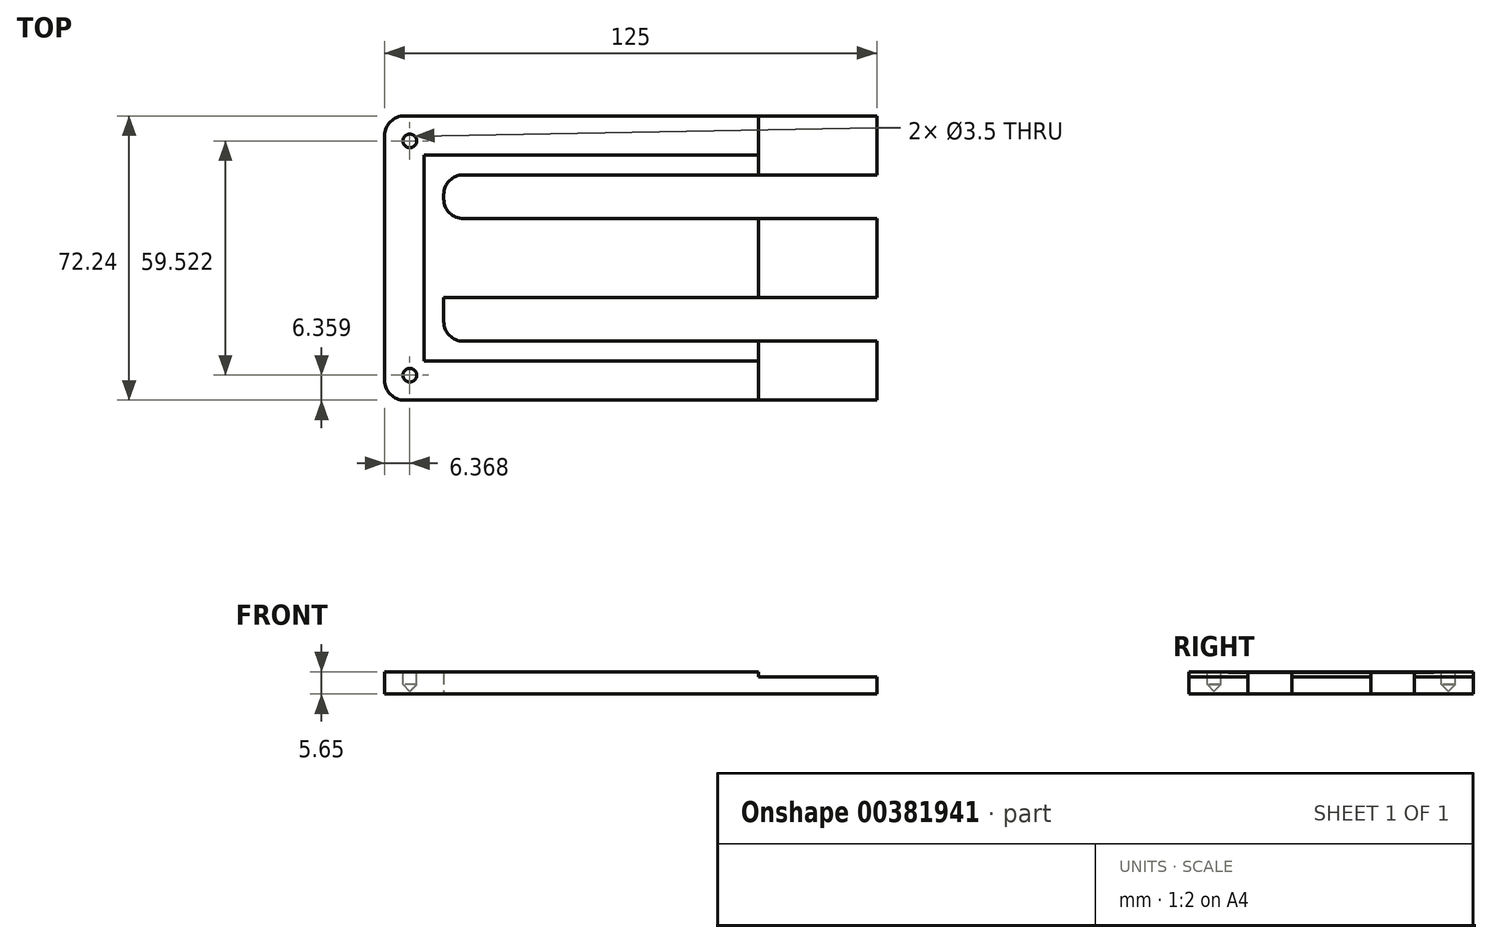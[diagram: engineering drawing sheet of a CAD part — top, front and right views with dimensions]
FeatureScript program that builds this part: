
annotation { "Feature Type Name" : "Feature", "Feature Type Description" : "" }
export const myFeature = defineFeature(function(context is Context, id is Id, definition is map)
    precondition{}
    {
        {
            var Q0;
            Q0=qCreatedBy(makeId("Top.planeOp"),FACE);
            var sketch = newSketch(context, id + "F0", { "sketchPlane" : qUnion([Q0])});
            skLineSegment(sketch, "E0.bottom", {"start": v(-143.35, 36.12) * mm, "end": v(86.65, 36.13) * mm});
            skLineSegment(sketch, "E0.top", {"start": v(-143.35, -36.13) * mm, "end": v(86.65, -36.12) * mm});
            skLineSegment(sketch, "E0.left", {"start": v(-143.35, 36.12) * mm, "end": v(-143.35, -36.13) * mm});
            skLineSegment(sketch, "E0.right", {"start": v(86.65, 36.13) * mm, "end": v(86.65, -36.12) * mm});
            skLineSegment(sketch, "E1.bottom", {"start": v(-128.35, 21.12) * mm, "end": v(71.65, 21.13) * mm});
            skLineSegment(sketch, "E1.top", {"start": v(-128.35, -21.13) * mm, "end": v(71.65, -21.12) * mm});
            skLineSegment(sketch, "E1.left", {"start": v(-128.35, 21.12) * mm, "end": v(-128.35, -21.13) * mm});
            skLineSegment(sketch, "E1.right", {"start": v(71.65, 21.13) * mm, "end": v(71.65, -21.12) * mm});
            skLineSegment(sketch, "E2.bottom", {"start": v(-133.35, 26.12) * mm, "end": v(76.65, 26.13) * mm});
            skLineSegment(sketch, "E2.top", {"start": v(-133.35, -26.13) * mm, "end": v(76.65, -26.12) * mm});
            skLineSegment(sketch, "E2.left", {"start": v(-133.35, 26.12) * mm, "end": v(-133.35, -26.13) * mm});
            skLineSegment(sketch, "E2.right", {"start": v(76.65, 26.13) * mm, "end": v(76.65, -26.12) * mm});
            skSolve(sketch);
        }
        {
            var Q0;
            Q0=makeQuery(id+"F0.imprint","IMPRINT",FACE,{"disambiguationData":[TD([[makeQuery(id+"F0.imprint","IMPRINT",EDGE,{"derivedFrom":sQuery(id+"F0.wireOp",EDGE,"E1.bottom")}),1.0]])]});
            extrude(context, id + "F1", {"entities" : qUnion([Q0]), "depth" : 5.5 * mm});
        }
        {
            var Q0;
            Q0=makeQuery(id+"F0.imprint","IMPRINT",FACE,{"disambiguationData":[TD([[makeQuery(id+"F0.imprint","IMPRINT",EDGE,{"derivedFrom":sQuery(id+"F0.wireOp",EDGE,"E0.bottom")}),-1.0]])]});
            extrude(context, id + "F2", {"entities" : qUnion([Q0]), "operationType" : NewBodyOperationType.ADD, "depth" : 5.65 * mm});
        }
        {
            var Q0;
            Q0=makeQuery(id+"F2.opExtrude","SWEPT_FACE",FACE,{"disambiguationData":[OSD([sQuery(id+"F0.wireOp",EDGE,"E0.top")])]});
            var sketch = newSketch(context, id + "F3", { "sketchPlane" : qUnion([Q0])});
            skPoint(sketch, "E3.orphan", {"position": v(66.65, 1.3) * mm});
            skPoint(sketch, "E4.start.orphan", {"position": v(-133.35, 1.3) * mm});
            skLineSegment(sketch, "E5", {"start": v(-48.35, 4.35) * mm, "end": v(-48.35, 5.65) * mm});
            skLineSegment(sketch, "E6", {"start": v(-18.35, 4.35) * mm, "end": v(-18.35, 0) * mm});
            skPoint(sketch, "E7.start.orphan", {"position": v(-13.35, 1.3) * mm});
            skPoint(sketch, "E8.end.orphan", {"position": v(-28.35, 5.65) * mm});
            skPoint(sketch, "E9.start.orphan", {"position": v(-33.35, 1.3) * mm});
            skLineSegment(sketch, "E10", {"start": v(-48.35, 4.35) * mm, "end": v(-18.35, 4.35) * mm});
            skSolve(sketch);
        }
        {
            var Q0;
            {var subQ3=sQuery(id+"F3.wireOp",EDGE,"E5");Q0=makeQuery(id+"F3.imprint","IMPRINT",FACE,{"disambiguationData":[TD([[makeQuery(id+"F3.imprint","IMPRINT",EDGE,{"derivedFrom":subQ3}),-1.0]])]});}
            extrude(context, id + "F4", {"entities" : qUnion([Q0]), "operationType" : NewBodyOperationType.REMOVE, "oppositeDirection" : true, "depth" : 100 * mm});
        }
        {
            var Q0;
            Q0=makeQuery(id+"F2.opExtrude","CAP_FACE",FACE,{"disambiguationData":[OSD([sQuery(id+"F0.wireOp",EDGE,"E0.bottom"),sQuery(id+"F0.wireOp",EDGE,"E0.top"),sQuery(id+"F0.wireOp",EDGE,"E0.left"),sQuery(id+"F0.wireOp",EDGE,"E0.right"),sQuery(id+"F0.wireOp",EDGE,"E2.bottom"),sQuery(id+"F0.wireOp",EDGE,"E2.top"),sQuery(id+"F0.wireOp",EDGE,"E2.left"),sQuery(id+"F0.wireOp",EDGE,"E2.right")])],"isStart":false});
            var sketch = newSketch(context, id + "F5", { "sketchPlane" : qUnion([Q0])});
            skLineSegment(sketch, "E11", {"start": v(-143.35, -36.13) * mm, "end": v(-133.35, -26.13) * mm});
            skCircle(sketch, "E12", {"center": v(-136.98, -29.76) * mm, "radius": 1.75 * mm});
            skLineSegment(sketch, "E13.MirrorCS", {"start": v(-143.35, 36.13) * mm, "end": v(-133.35, 26.13) * mm});
            skCircle(sketch, "E14.MirrorC", {"center": v(-136.98, 29.76) * mm, "radius": 1.75 * mm});
            skSolve(sketch);
        }
        {
            var Q0;
            {var subQ0=sQuery(id+"F5.wireOp",EDGE,"E14.MirrorC");var subQ1=sQuery(id+"F5.wireOp",EDGE,"E13.MirrorCS");var subQ2=makeQuery(id+"F5.imprint","INTERSECT",VERTEX,{"disambiguationData":[OD(0.0)],"derivedFrom":[subQ1,subQ0]});Q0=makeQuery(id+"F5.imprint","IMPRINT",FACE,{"disambiguationData":[TD([[makeQuery(id+"F5.imprint","IMPRINT",EDGE,{"disambiguationData":[TD([[subQ2,-1.0]])],"derivedFrom":subQ1}),1.0]])]});}
            var Q1;
            {var subQ0=sQuery(id+"F5.wireOp",EDGE,"E14.MirrorC");var subQ1=sQuery(id+"F5.wireOp",EDGE,"E13.MirrorCS");var subQ2=makeQuery(id+"F5.imprint","INTERSECT",VERTEX,{"disambiguationData":[OD(0.0)],"derivedFrom":[subQ1,subQ0]});Q1=makeQuery(id+"F5.imprint","IMPRINT",FACE,{"disambiguationData":[TD([[makeQuery(id+"F5.imprint","IMPRINT",EDGE,{"disambiguationData":[TD([[subQ2,-1.0]])],"derivedFrom":subQ1}),-1.0]])]});}
            var Q2;
            {var subQ0=sQuery(id+"F5.wireOp",EDGE,"E12");var subQ1=sQuery(id+"F5.wireOp",EDGE,"E11");var subQ2=makeQuery(id+"F5.imprint","INTERSECT",VERTEX,{"disambiguationData":[OD(0.0)],"derivedFrom":[subQ1,subQ0]});Q2=makeQuery(id+"F5.imprint","IMPRINT",FACE,{"disambiguationData":[TD([[makeQuery(id+"F5.imprint","IMPRINT",EDGE,{"disambiguationData":[TD([[subQ2,-1.0]])],"derivedFrom":subQ1}),1.0]])]});}
            var Q3;
            {var subQ0=sQuery(id+"F5.wireOp",EDGE,"E12");var subQ1=sQuery(id+"F5.wireOp",EDGE,"E11");var subQ2=makeQuery(id+"F5.imprint","INTERSECT",VERTEX,{"disambiguationData":[OD(0.0)],"derivedFrom":[subQ1,subQ0]});Q3=makeQuery(id+"F5.imprint","IMPRINT",FACE,{"disambiguationData":[TD([[makeQuery(id+"F5.imprint","IMPRINT",EDGE,{"disambiguationData":[TD([[subQ2,-1.0]])],"derivedFrom":subQ1}),-1.0]])]});}
            extrude(context, id + "F6", {"entities" : qUnion([Q0, Q1, Q2, Q3]), "operationType" : NewBodyOperationType.REMOVE, "oppositeDirection" : true, "depth" : 5 * mm});
        }
        {
            var Q0;
            Q0=makeQuery(id+"F6.boolean.opBoolean","COPY",EDGE,{"derivedFrom":makeQuery(id+"F6.opExtrude","CAP_EDGE",EDGE,{"disambiguationData":[OSD([sQuery(id+"F5.wireOp",EDGE,"E12")])],"isStart":false})});
            var Q1;
            Q1=makeQuery(id+"F6.boolean.opBoolean","COPY",EDGE,{"derivedFrom":makeQuery(id+"F6.opExtrude","CAP_EDGE",EDGE,{"disambiguationData":[OSD([sQuery(id+"F5.wireOp",EDGE,"E14.MirrorC")])],"isStart":false})});
            chamfer(context, id + "F7", {"entities" : qUnion([Q0, Q1]), "width" : 1.75 * mm, "tangentPropagation" : true});
        }
        {
            var Q0;
            Q0=makeQuery(id+"F2.opExtrude","SWEPT_EDGE",EDGE,{"disambiguationData":[OSD([sQuery(id+"F0.wireOp",EDGE,"E0.bottom"),sQuery(id+"F0.wireOp",EDGE,"E0.left")])]});
            var Q1;
            Q1=makeQuery(id+"F2.opExtrude","SWEPT_EDGE",EDGE,{"disambiguationData":[OSD([sQuery(id+"F0.wireOp",EDGE,"E0.top"),sQuery(id+"F0.wireOp",EDGE,"E0.left")])]});
            fillet(context, id + "F8", {"entities" : qUnion([Q0, Q1]), "radius" : 5 * mm, "tangentPropagation" : true, "allowEdgeOverflow" : false});
        }
        {
            var Q0;
            Q0=makeQuery(id+"F1.opExtrude","SWEPT_EDGE",EDGE,{"disambiguationData":[OSD([sQuery(id+"F0.wireOp",EDGE,"E1.top"),sQuery(id+"F0.wireOp",EDGE,"E1.left")])]});
            var Q1;
            Q1=makeQuery(id+"F1.opExtrude","SWEPT_EDGE",EDGE,{"disambiguationData":[OSD([sQuery(id+"F0.wireOp",EDGE,"E1.bottom"),sQuery(id+"F0.wireOp",EDGE,"E1.left")])]});
            fillet(context, id + "F9", {"entities" : qUnion([Q0, Q1]), "radius" : 5 * mm, "tangentPropagation" : true, "allowEdgeOverflow" : false});
        }
        {
            var Q0;
            Q0=makeQuery(id+"F1.opExtrude","SWEPT_FACE",FACE,{"disambiguationData":[OSD([sQuery(id+"F0.wireOp",EDGE,"E1.left")])]});
            var sketch = newSketch(context, id + "F10", { "sketchPlane" : qUnion([Q0])});
            skLineSegment(sketch, "E15.bottom", {"start": v(-10, 5.5) * mm, "end": v(10, 5.5) * mm});
            skLineSegment(sketch, "E15.top", {"start": v(-10, 0) * mm, "end": v(10, 0) * mm});
            skLineSegment(sketch, "E15.left", {"start": v(-10, 5.5) * mm, "end": v(-10, 0) * mm});
            skLineSegment(sketch, "E15.right", {"start": v(10, 5.5) * mm, "end": v(10, 0) * mm});
            skSolve(sketch);
        }
        {
            var Q0;
            Q0=makeQuery(id+"F10.imprint","IMPRINT",FACE,{"disambiguationData":[TD([[makeQuery(id+"F10.imprint","IMPRINT",EDGE,{"derivedFrom":sQuery(id+"F10.wireOp",EDGE,"E15.bottom")}),1.0]])]});
            extrude(context, id + "F11", {"entities" : qUnion([Q0]), "operationType" : NewBodyOperationType.ADD, "depth" : 110 * mm});
        }
        {
            var Q0;
            Q0=makeQuery(id+"F11.opExtrude","SWEPT_FACE",FACE,{"disambiguationData":[OSD([sQuery(id+"F10.wireOp",EDGE,"E15.left")])]});
            var sketch = newSketch(context, id + "F12", { "sketchPlane" : qUnion([Q0])});
            skLineSegment(sketch, "E16.bottom", {"start": v(-18.35, 4.35) * mm, "end": v(-48.35, 4.35) * mm});
            skLineSegment(sketch, "E16.top", {"start": v(-18.35, 5.5) * mm, "end": v(-48.35, 5.5) * mm});
            skLineSegment(sketch, "E16.left", {"start": v(-18.35, 4.35) * mm, "end": v(-18.35, 5.5) * mm});
            skLineSegment(sketch, "E16.right", {"start": v(-48.35, 4.35) * mm, "end": v(-48.35, 5.5) * mm});
            skSolve(sketch);
        }
        {
            var Q0;
            Q0=makeQuery(id+"F12.imprint","IMPRINT",FACE,{"disambiguationData":[TD([[makeQuery(id+"F12.imprint","IMPRINT",EDGE,{"derivedFrom":sQuery(id+"F12.wireOp",EDGE,"E16.bottom")}),-1.0]])]});
            extrude(context, id + "F13", {"entities" : qUnion([Q0]), "operationType" : NewBodyOperationType.REMOVE, "oppositeDirection" : true, "depth" : 25 * mm});
        }
        {
            var Q0;
            Q0=makeQuery(id+"F11.opExtrude","CAP_EDGE",EDGE,{"disambiguationData":[OSD([sQuery(id+"F10.wireOp",EDGE,"E15.left")])],"isStart":true});
            var Q1;
            Q1=makeQuery(id+"F11.opExtrude","CAP_EDGE",EDGE,{"disambiguationData":[OSD([sQuery(id+"F10.wireOp",EDGE,"E15.right")])],"isStart":true});
            fillet(context, id + "F14", {"entities" : qUnion([Q0, Q1]), "radius" : 5 * mm, "tangentPropagation" : true, "allowEdgeOverflow" : false});
        }
    });
